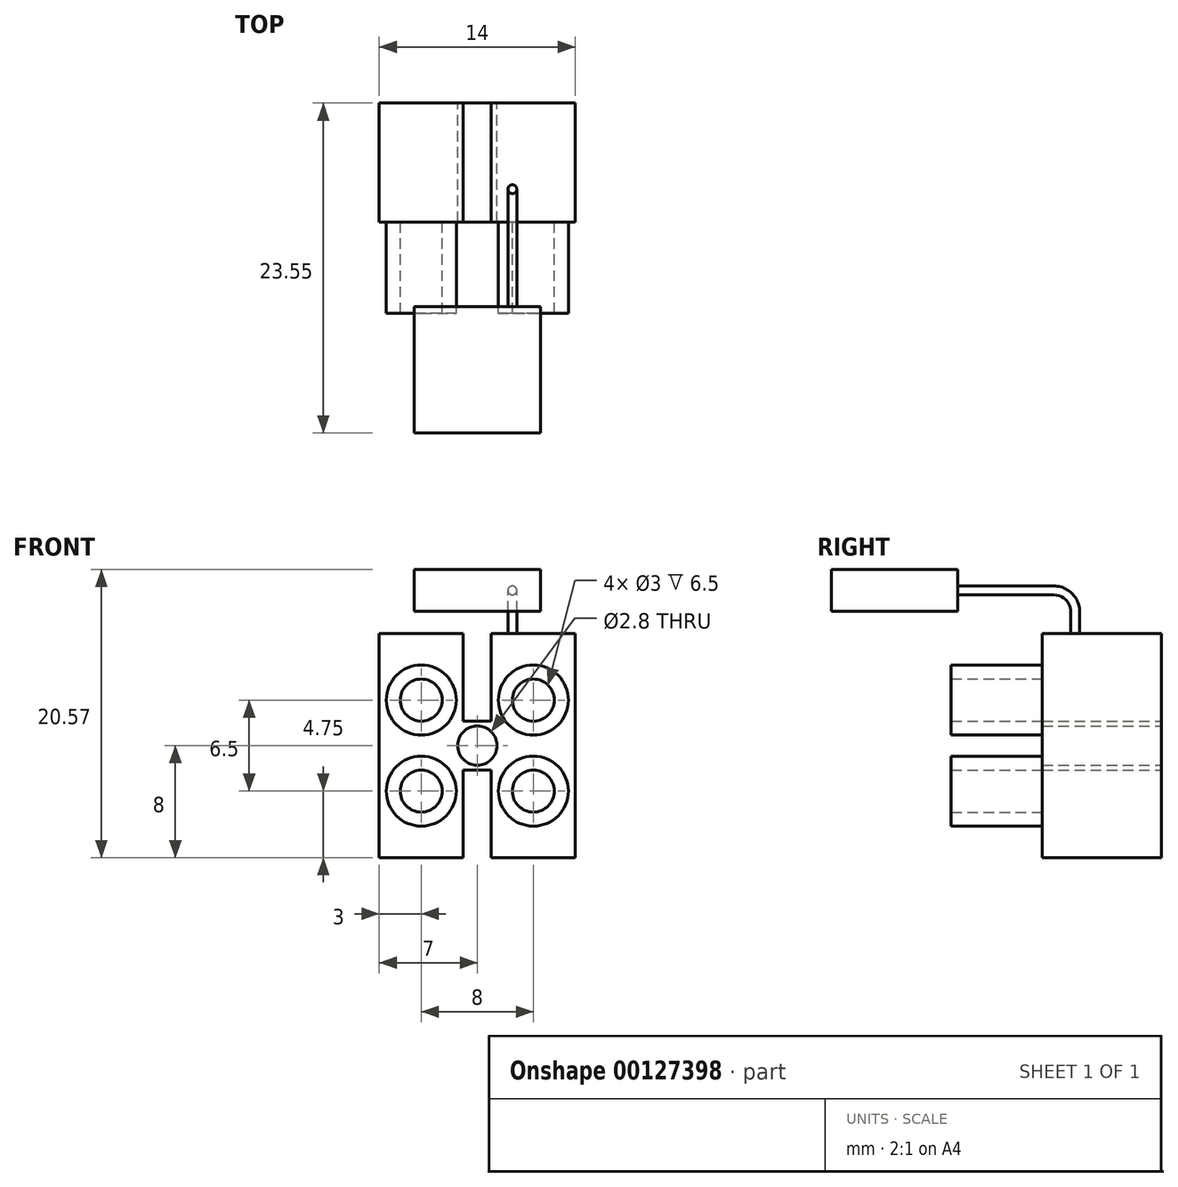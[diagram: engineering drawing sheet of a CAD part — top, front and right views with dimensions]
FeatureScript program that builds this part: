
annotation { "Feature Type Name" : "Feature", "Feature Type Description" : "" }
export const myFeature = defineFeature(function(context is Context, id is Id, definition is map)
    precondition{}
    {
        {
            var Q0;
            Q0=qCreatedBy(makeId("Front.planeOp"),FACE);
            var sketch = newSketch(context, id + "F0", { "sketchPlane" : qUnion([Q0])});
            skLineSegment(sketch, "E0.bottom", {"start": v(-7, 8) * mm, "end": v(-1, 8) * mm});
            skLineSegment(sketch, "E0.top", {"start": v(-7, -8) * mm, "end": v(-1, -8) * mm});
            skLineSegment(sketch, "E0.left", {"start": v(-7, 8) * mm, "end": v(-7, -8) * mm});
            skLineSegment(sketch, "E0.right", {"start": v(7, 8) * mm, "end": v(7, -8) * mm});
            skPoint(sketch, "E0.middle", {"position": v(0, 0) * mm});
            skLineSegment(sketch, "E1.bottom", {"start": v(1, 1.75) * mm, "end": v(-1, 1.75) * mm});
            skLineSegment(sketch, "E1.left", {"start": v(1, 1.75) * mm, "end": v(1, 8) * mm});
            skLineSegment(sketch, "E1.right", {"start": v(-1, 1.75) * mm, "end": v(-1, 8) * mm});
            skPoint(sketch, "E1.middle", {"position": v(0, 8) * mm});
            skLineSegment(sketch, "E2.MirrorCS", {"start": v(1, -1.75) * mm, "end": v(-1, -1.75) * mm});
            skLineSegment(sketch, "E3.MirrorCS", {"start": v(-1, -1.75) * mm, "end": v(-1, -8) * mm});
            skLineSegment(sketch, "E4.MirrorCS", {"start": v(1, -1.75) * mm, "end": v(1, -8) * mm});
            skPoint(sketch, "E5.MirrorP", {"position": v(0, -8) * mm});
            skPoint(sketch, "E1.top.end.orphan", {"position": v(-1, 14.25) * mm});
            skPoint(sketch, "E1.top.start.orphan", {"position": v(1, 14.25) * mm});
            skLineSegment(sketch, "E6.trimOffspring", {"start": v(1, 8) * mm, "end": v(7, 8) * mm});
            skPoint(sketch, "E7.MirrorCS.end.orphan", {"position": v(-1, -14.25) * mm});
            skPoint(sketch, "E7.MirrorCS.start.orphan", {"position": v(1, -14.25) * mm});
            skLineSegment(sketch, "E8.trimOffspring", {"start": v(1, -8) * mm, "end": v(7, -8) * mm});
            skCircle(sketch, "E9", {"center": v(0, 0) * mm, "radius": 1.4 * mm});
            skPoint(sketch, "E10", {"position": v(-4, 8) * mm});
            skSolve(sketch);
        }
        {
            var Q0;
            Q0 = qSketchRegion(id + "F0", true);
            extrude(context, id + "F1", {"entities" : qUnion([Q0]), "depth" : 8.5 * mm});
        }
        {
            var Q0;
            Q0=makeQuery(id+"F1.opExtrude","CAP_FACE",FACE,{"disambiguationData":[OSD([sQuery(id+"F0.wireOp",EDGE,"E0.bottom"),sQuery(id+"F0.wireOp",EDGE,"E0.top"),sQuery(id+"F0.wireOp",EDGE,"E0.left"),sQuery(id+"F0.wireOp",EDGE,"E0.right"),sQuery(id+"F0.wireOp",EDGE,"E1.bottom"),sQuery(id+"F0.wireOp",EDGE,"E1.left"),sQuery(id+"F0.wireOp",EDGE,"E1.right"),sQuery(id+"F0.wireOp",EDGE,"E2.MirrorCS"),sQuery(id+"F0.wireOp",EDGE,"E3.MirrorCS"),sQuery(id+"F0.wireOp",EDGE,"E4.MirrorCS"),sQuery(id+"F0.wireOp",EDGE,"E6.trimOffspring"),sQuery(id+"F0.wireOp",EDGE,"E8.trimOffspring"),sQuery(id+"F0.wireOp",EDGE,"E9")])],"isStart":false});
            var sketch = newSketch(context, id + "F2", { "sketchPlane" : qUnion([Q0])});
            skCircle(sketch, "E11", {"center": v(-4, 3.25) * mm, "radius": 1.5 * mm});
            skCircle(sketch, "E12", {"center": v(-4, 3.25) * mm, "radius": 2.5 * mm});
            skCircle(sketch, "E13.MirrorC", {"center": v(-4, -3.25) * mm, "radius": 1.5 * mm});
            skCircle(sketch, "E14.MirrorC", {"center": v(-4, -3.25) * mm, "radius": 2.5 * mm});
            skCircle(sketch, "E15.MirrorC", {"center": v(4, -3.25) * mm, "radius": 1.5 * mm});
            skCircle(sketch, "E16.MirrorC", {"center": v(4, 3.25) * mm, "radius": 2.5 * mm});
            skCircle(sketch, "E17.MirrorC", {"center": v(4, 3.25) * mm, "radius": 1.5 * mm});
            skCircle(sketch, "E18.MirrorC", {"center": v(4, -3.25) * mm, "radius": 2.5 * mm});
            skSolve(sketch);
        }
        {
            var Q0;
            Q0 = qSketchRegion(id + "F2", true);
            extrude(context, id + "F3", {"entities" : qUnion([Q0]), "operationType" : NewBodyOperationType.ADD, "depth" : 6.5 * mm});
        }
        {
            var Q0;
            Q0=makeQuery(id+"F1.opExtrude","SWEPT_FACE",FACE,{"disambiguationData":[OSD([sQuery(id+"F0.wireOp",EDGE,"E0.bottom")])]});
            cPlane(context, id + "F4", {"entities" : qUnion([Q0]), "cplaneType" : CPlaneType.OFFSET, "offset" : 1.57 * mm, "width" : 152.4 * mm, "height" : 152.4 * mm});
        }
        {
            var Q0;
            Q0=qCreatedBy(id+"F4.planeOp",FACE);
            var sketch = newSketch(context, id + "F5", { "sketchPlane" : qUnion([Q0])});
            skLineSegment(sketch, "E19.bottom", {"start": v(-4.5, -14.55) * mm, "end": v(4.5, -14.55) * mm});
            skLineSegment(sketch, "E19.top", {"start": v(-4.5, -23.55) * mm, "end": v(4.5, -23.55) * mm});
            skLineSegment(sketch, "E19.left", {"start": v(-4.5, -14.55) * mm, "end": v(-4.5, -23.55) * mm});
            skLineSegment(sketch, "E19.right", {"start": v(4.5, -14.55) * mm, "end": v(4.5, -23.55) * mm});
            skPoint(sketch, "E19.middle", {"position": v(0, -19.05) * mm});
            skSolve(sketch);
        }
        {
            var Q0;
            Q0 = qSketchRegion(id + "F5", true);
            extrude(context, id + "F6", {"entities" : qUnion([Q0]), "operationType" : NewBodyOperationType.ADD, "depth" : 3 * mm});
        }
        {
            var Q0;
            Q0=qCreatedBy(makeId("Right.planeOp"),FACE);
            cPlane(context, id + "F7", {"entities" : qUnion([Q0]), "cplaneType" : CPlaneType.OFFSET, "offset" : 2.5 * mm, "width" : 152.4 * mm, "height" : 152.4 * mm});
        }
        {
            var Q0;
            Q0=qCreatedBy(id+"F7.planeOp",FACE);
            var sketch = newSketch(context, id + "F8", { "sketchPlane" : qUnion([Q0])});
            skLineSegment(sketch, "E20", {"start": v(-14.55, 12.57) * mm, "end": v(-14.55, 9.57) * mm, "construction": true});
            skPoint(sketch, "E21", {"position": v(-14.55, 11.07) * mm});
            skLineSegment(sketch, "E22", {"start": v(-14.55, 11.07) * mm, "end": v(-7.68, 11.07) * mm});
            skLineSegment(sketch, "E23", {"start": v(-6.15, 9.55) * mm, "end": v(-6.15, 7.98) * mm});
            skPoint(sketch, "E24.visualSharp", {"position": v(-6.15, 11.07) * mm});
            skArc(sketch, "E24.filletArc", {"start": v(-6.15, 9.55) * mm, "mid": v(-6.6, 10.63) * mm, "end": v(-7.68, 11.07) * mm});
            skSolve(sketch);
        }
        {
            var Q0;
            Q0=makeQuery(id+"F6.opExtrude","SWEPT_FACE",FACE,{"disambiguationData":[OSD([sQuery(id+"F5.wireOp",EDGE,"E19.bottom")])]});
            var sketch = newSketch(context, id + "F9", { "sketchPlane" : qUnion([Q0])});
            skCircle(sketch, "E25", {"center": v(-2.5, 11.07) * mm, "radius": 0.32 * mm});
            skSolve(sketch);
        }
        {
            var Q0;
            Q0=makeQuery(id+"F9.imprint","IMPRINT",FACE,{"disambiguationData":[TD([[makeQuery(id+"F9.imprint","IMPRINT",EDGE,{"derivedFrom":sQuery(id+"F9.wireOp",EDGE,"E25")}),1.0]])]});
            var Q1;
            Q1=sQuery(id+"F8.wireOp",EDGE,"E22");
            var Q2;
            Q2=sQuery(id+"F8.wireOp",EDGE,"E24.filletArc");
            var Q3;
            Q3=sQuery(id+"F8.wireOp",EDGE,"E23");
            sweep(context, id + "F10", {"operationType" : NewBodyOperationType.ADD, "profiles" : qUnion([Q0]), "path" : qUnion([Q1, Q2, Q3])});
        }
    });
